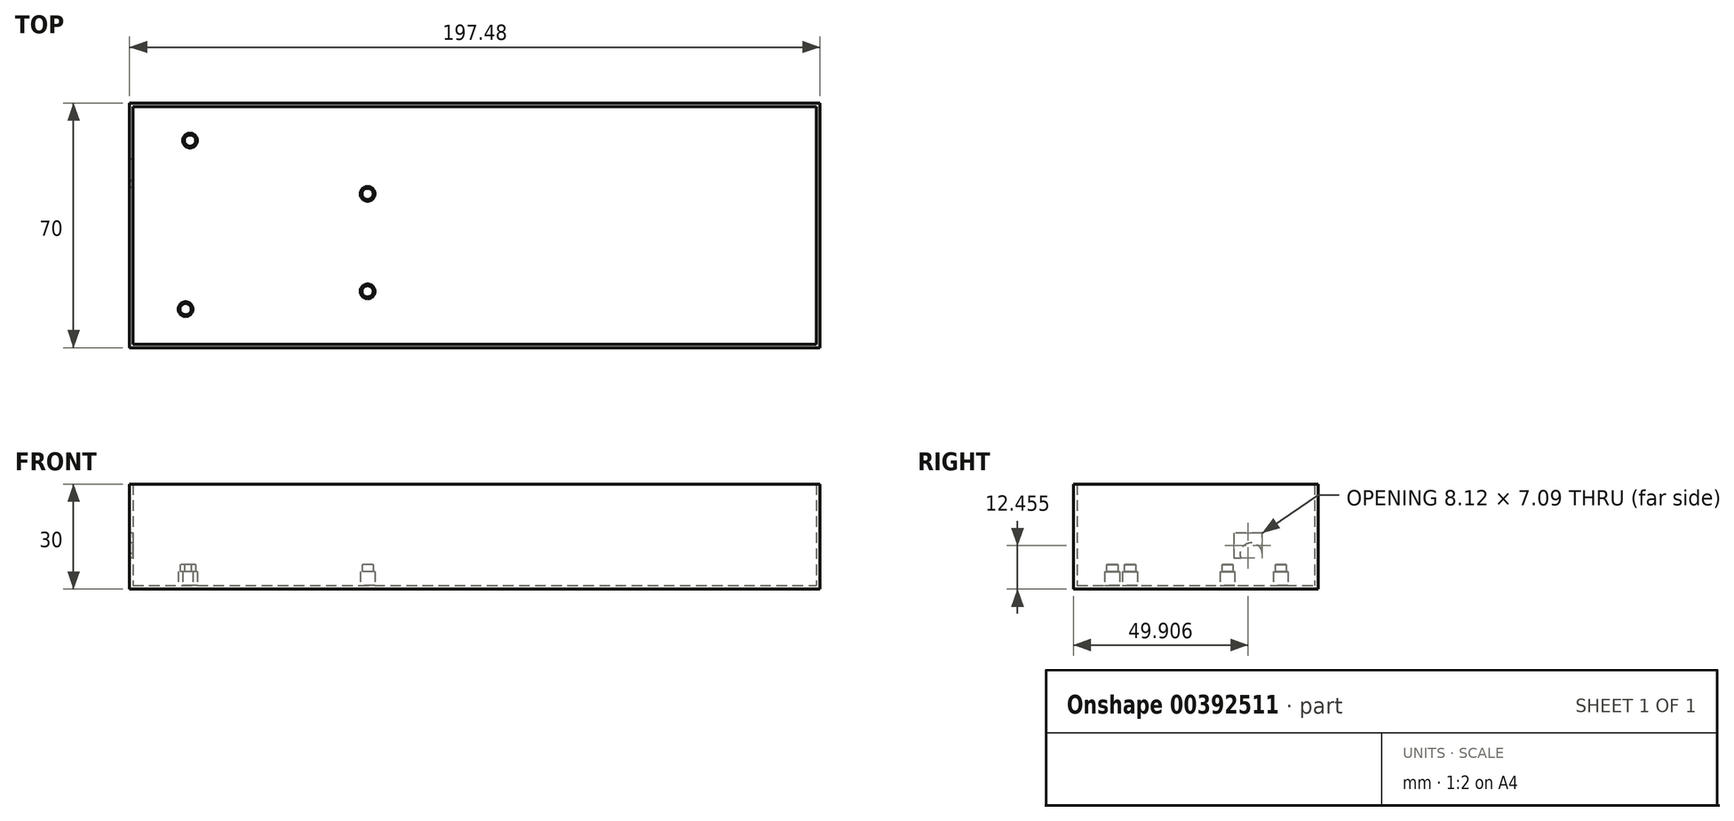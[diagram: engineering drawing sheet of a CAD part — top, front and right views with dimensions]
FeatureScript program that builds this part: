
annotation { "Feature Type Name" : "Feature", "Feature Type Description" : "" }
export const myFeature = defineFeature(function(context is Context, id is Id, definition is map)
    precondition{}
    {
        {
            var Q0;
            Q0=qCreatedBy(makeId("Top.planeOp"),FACE);
            var sketch = newSketch(context, id + "F0", { "sketchPlane" : qUnion([Q0])});
            skLineSegment(sketch, "E0", {"start": v(5.58, 61.8) * mm, "end": v(69.06, 61.8) * mm});
            skLineSegment(sketch, "E1", {"start": v(5.33, 61.76) * mm, "end": v(5.58, 61.8) * mm});
            skLineSegment(sketch, "E2", {"start": v(5.1, 61.65) * mm, "end": v(5.33, 61.76) * mm});
            skLineSegment(sketch, "E3", {"start": v(4.88, 61.5) * mm, "end": v(5.1, 61.65) * mm});
            skLineSegment(sketch, "E4", {"start": v(4.71, 61.3) * mm, "end": v(4.88, 61.5) * mm});
            skLineSegment(sketch, "E5", {"start": v(4.63, 61.06) * mm, "end": v(4.71, 61.3) * mm});
            skLineSegment(sketch, "E6", {"start": v(4.59, 60.79) * mm, "end": v(4.63, 61.06) * mm});
            skLineSegment(sketch, "E7", {"start": v(4.59, 9.5) * mm, "end": v(4.59, 60.79) * mm});
            skLineSegment(sketch, "E8", {"start": v(4.63, 9.24) * mm, "end": v(4.59, 9.5) * mm});
            skLineSegment(sketch, "E9", {"start": v(4.71, 9) * mm, "end": v(4.63, 9.24) * mm});
            skLineSegment(sketch, "E10", {"start": v(4.88, 8.8) * mm, "end": v(4.71, 9) * mm});
            skLineSegment(sketch, "E11", {"start": v(5.1, 8.63) * mm, "end": v(4.88, 8.8) * mm});
            skLineSegment(sketch, "E12", {"start": v(5.33, 8.54) * mm, "end": v(5.1, 8.63) * mm});
            skLineSegment(sketch, "E13", {"start": v(5.58, 8.5) * mm, "end": v(5.33, 8.54) * mm});
            skLineSegment(sketch, "E14", {"start": v(69.59, 8.5) * mm, "end": v(5.58, 8.5) * mm});
            skLineSegment(sketch, "E15", {"start": v(69.84, 8.54) * mm, "end": v(69.59, 8.5) * mm});
            skLineSegment(sketch, "E16", {"start": v(70.07, 8.63) * mm, "end": v(69.84, 8.54) * mm});
            skLineSegment(sketch, "E17", {"start": v(70.29, 8.8) * mm, "end": v(70.07, 8.63) * mm});
            skLineSegment(sketch, "E18", {"start": v(70.46, 9) * mm, "end": v(70.29, 8.8) * mm});
            skLineSegment(sketch, "E19", {"start": v(70.54, 9.24) * mm, "end": v(70.46, 9) * mm});
            skLineSegment(sketch, "E20", {"start": v(70.58, 9.5) * mm, "end": v(70.54, 9.24) * mm});
            skLineSegment(sketch, "E21", {"start": v(70.58, 11.04) * mm, "end": v(70.58, 9.5) * mm});
            skLineSegment(sketch, "E22", {"start": v(73.12, 13.58) * mm, "end": v(70.58, 11.04) * mm});
            skLineSegment(sketch, "E23", {"start": v(73.12, 46.31) * mm, "end": v(73.12, 13.58) * mm});
            skLineSegment(sketch, "E24", {"start": v(70.58, 48.85) * mm, "end": v(73.12, 46.31) * mm});
            skLineSegment(sketch, "E25", {"start": v(70.58, 60.28) * mm, "end": v(70.58, 48.85) * mm});
            skLineSegment(sketch, "E26", {"start": v(69.06, 61.8) * mm, "end": v(70.58, 60.28) * mm});
            skCircle(sketch, "E27", {"center": v(19.82, 59.26) * mm, "radius": 1.6 * mm});
            skCircle(sketch, "E28", {"center": v(70.58, 44.03) * mm, "radius": 1.6 * mm});
            skCircle(sketch, "E29", {"center": v(70.58, 16.12) * mm, "radius": 1.6 * mm});
            skCircle(sketch, "E30", {"center": v(18.55, 11.04) * mm, "radius": 1.6 * mm});
            skSolve(sketch);
        }
        {
            var Q0;
            Q0=qCreatedBy(makeId("Top.planeOp"),FACE);
            var sketch = newSketch(context, id + "F1", { "sketchPlane" : qUnion([Q0])});
            skLineSegment(sketch, "E31", {"start": v(-3.83, 44.58) * mm, "end": v(3.97, 44.58) * mm});
            skLineSegment(sketch, "E32", {"start": v(3.97, 44.58) * mm, "end": v(3.97, 36.46) * mm});
            skLineSegment(sketch, "E33", {"start": v(3.97, 36.46) * mm, "end": v(-3.83, 36.46) * mm});
            skLineSegment(sketch, "E34", {"start": v(-3.83, 36.46) * mm, "end": v(-3.83, 44.58) * mm});
            skLineSegment(sketch, "E35", {"start": v(-3.79, 49.08) * mm, "end": v(1.44, 49.08) * mm});
            skLineSegment(sketch, "E36", {"start": v(1.44, 50.7) * mm, "end": v(-3.79, 50.7) * mm});
            skLineSegment(sketch, "E37", {"start": v(-3.79, 47.45) * mm, "end": v(1.44, 47.45) * mm});
            skLineSegment(sketch, "E38", {"start": v(1.44, 45.85) * mm, "end": v(-3.79, 45.85) * mm});
            skLineSegment(sketch, "E39", {"start": v(-3.79, 52.34) * mm, "end": v(1.44, 52.34) * mm});
            skLineSegment(sketch, "E40", {"start": v(1.44, 53.97) * mm, "end": v(-3.79, 53.97) * mm});
            skLineSegment(sketch, "E41", {"start": v(-3.79, 55.17) * mm, "end": v(-3.79, 53.97) * mm});
            skLineSegment(sketch, "E42", {"start": v(-3.79, 53.97) * mm, "end": v(-3.79, 52.34) * mm});
            skLineSegment(sketch, "E43", {"start": v(-3.79, 52.34) * mm, "end": v(-3.79, 50.7) * mm});
            skLineSegment(sketch, "E44", {"start": v(-3.79, 50.7) * mm, "end": v(-3.79, 49.08) * mm});
            skLineSegment(sketch, "E45", {"start": v(-3.79, 49.08) * mm, "end": v(-3.79, 47.45) * mm});
            skLineSegment(sketch, "E46", {"start": v(-3.79, 47.45) * mm, "end": v(-3.79, 45.85) * mm});
            skLineSegment(sketch, "E47", {"start": v(-3.79, 45.85) * mm, "end": v(-3.79, 44.62) * mm});
            skLineSegment(sketch, "E48", {"start": v(-3.79, 44.62) * mm, "end": v(-5.18, 44.62) * mm});
            skLineSegment(sketch, "E49", {"start": v(-5.18, 44.62) * mm, "end": v(-5.18, 45.85) * mm});
            skLineSegment(sketch, "E50", {"start": v(-5.18, 45.85) * mm, "end": v(-5.18, 53.97) * mm});
            skLineSegment(sketch, "E51", {"start": v(-5.18, 53.97) * mm, "end": v(-5.18, 55.17) * mm});
            skLineSegment(sketch, "E52", {"start": v(-5.18, 55.17) * mm, "end": v(-3.79, 55.17) * mm});
            skLineSegment(sketch, "E53", {"start": v(-5.18, 45.85) * mm, "end": v(-6.81, 45.85) * mm});
            skLineSegment(sketch, "E54", {"start": v(-6.81, 45.85) * mm, "end": v(-7.68, 45.85) * mm});
            skLineSegment(sketch, "E55", {"start": v(-7.68, 45.85) * mm, "end": v(-8.08, 45.85) * mm});
            skLineSegment(sketch, "E56", {"start": v(-8.08, 45.85) * mm, "end": v(-8.44, 45.85) * mm});
            skLineSegment(sketch, "E57", {"start": v(-8.44, 45.85) * mm, "end": v(-8.88, 45.85) * mm});
            skLineSegment(sketch, "E58", {"start": v(-8.88, 45.85) * mm, "end": v(-9.29, 45.85) * mm});
            skLineSegment(sketch, "E59", {"start": v(-9.29, 45.85) * mm, "end": v(-9.7, 45.85) * mm});
            skLineSegment(sketch, "E60", {"start": v(-9.7, 45.85) * mm, "end": v(-10.07, 45.85) * mm});
            skLineSegment(sketch, "E61", {"start": v(-10.07, 45.85) * mm, "end": v(-10.51, 45.85) * mm});
            skLineSegment(sketch, "E62", {"start": v(-10.51, 45.85) * mm, "end": v(-10.91, 45.85) * mm});
            skLineSegment(sketch, "E63", {"start": v(-10.91, 45.85) * mm, "end": v(-11.68, 45.85) * mm});
            skLineSegment(sketch, "E64", {"start": v(-11.68, 45.85) * mm, "end": v(-14.17, 45.85) * mm});
            skLineSegment(sketch, "E65", {"start": v(-5.18, 53.97) * mm, "end": v(-8.08, 53.97) * mm});
            skLineSegment(sketch, "E66", {"start": v(-8.08, 53.97) * mm, "end": v(-8.88, 53.97) * mm});
            skLineSegment(sketch, "E67", {"start": v(-8.88, 53.97) * mm, "end": v(-9.7, 53.97) * mm});
            skLineSegment(sketch, "E68", {"start": v(-9.7, 53.97) * mm, "end": v(-10.51, 53.97) * mm});
            skLineSegment(sketch, "E69", {"start": v(-10.51, 53.97) * mm, "end": v(-11.32, 53.97) * mm});
            skLineSegment(sketch, "E70", {"start": v(-11.32, 53.97) * mm, "end": v(-12.14, 53.97) * mm});
            skLineSegment(sketch, "E71", {"start": v(-12.14, 53.97) * mm, "end": v(-12.95, 53.97) * mm});
            skLineSegment(sketch, "E72", {"start": v(-12.95, 53.97) * mm, "end": v(-14.17, 53.97) * mm});
            skLineSegment(sketch, "E73", {"start": v(-14.17, 45.85) * mm, "end": v(-14.17, 53.97) * mm});
            skLineSegment(sketch, "E74", {"start": v(-12.14, 53.97) * mm, "end": v(-10.87, 45.85) * mm});
            skLineSegment(sketch, "E75", {"start": v(-11.32, 53.97) * mm, "end": v(-10.07, 45.85) * mm});
            skLineSegment(sketch, "E76", {"start": v(-10.51, 53.97) * mm, "end": v(-9.24, 45.85) * mm});
            skLineSegment(sketch, "E77", {"start": v(-9.7, 53.97) * mm, "end": v(-8.44, 45.85) * mm});
            skLineSegment(sketch, "E78", {"start": v(-8.88, 53.97) * mm, "end": v(-7.62, 45.85) * mm});
            skLineSegment(sketch, "E79", {"start": v(-8.08, 53.97) * mm, "end": v(-6.81, 45.85) * mm});
            skLineSegment(sketch, "E80", {"start": v(-12.95, 53.97) * mm, "end": v(-11.68, 45.85) * mm});
            skLineSegment(sketch, "E81", {"start": v(-3.83, 34.95) * mm, "end": v(-3.83, 35.19) * mm});
            skLineSegment(sketch, "E82", {"start": v(-3.83, 35.19) * mm, "end": v(-3.83, 35.59) * mm});
            skLineSegment(sketch, "E83", {"start": v(-3.83, 35.59) * mm, "end": v(-2.2, 35.59) * mm});
            skLineSegment(sketch, "E84", {"start": v(0.04, 35.59) * mm, "end": v(0.8, 35.59) * mm});
            skLineSegment(sketch, "E85", {"start": v(0.8, 25.99) * mm, "end": v(0.04, 25.99) * mm});
            skLineSegment(sketch, "E86", {"start": v(-2.2, 25.99) * mm, "end": v(-3.83, 25.99) * mm});
            skLineSegment(sketch, "E87", {"start": v(-3.83, 25.99) * mm, "end": v(-3.83, 26.35) * mm});
            skLineSegment(sketch, "E88", {"start": v(-3.83, 26.35) * mm, "end": v(-3.83, 26.54) * mm});
            skLineSegment(sketch, "E89", {"start": v(-4.34, 34.55) * mm, "end": v(-4.34, 27.02) * mm});
            skLineSegment(sketch, "E90", {"start": v(-4.61, 34.55) * mm, "end": v(-4.61, 27.02) * mm});
            skLineSegment(sketch, "E91", {"start": v(-4.1, 34.7) * mm, "end": v(-4.06, 34.7) * mm});
            skLineSegment(sketch, "E92", {"start": v(-4.1, 34.7) * mm, "end": v(-4.42, 34.7) * mm});
            skLineSegment(sketch, "E93", {"start": v(-4.1, 26.8) * mm, "end": v(-4.06, 26.8) * mm});
            skLineSegment(sketch, "E94", {"start": v(-4.1, 26.8) * mm, "end": v(-4.42, 26.8) * mm});
            skLineSegment(sketch, "E95", {"start": v(-4.1, 34.7) * mm, "end": v(-3.98, 34.74) * mm});
            skLineSegment(sketch, "E96", {"start": v(-3.98, 34.74) * mm, "end": v(-3.83, 34.87) * mm});
            skLineSegment(sketch, "E97", {"start": v(-3.83, 34.87) * mm, "end": v(-3.83, 34.95) * mm});
            skLineSegment(sketch, "E98", {"start": v(-4.1, 34.7) * mm, "end": v(-4.23, 34.7) * mm});
            skLineSegment(sketch, "E99", {"start": v(-4.23, 34.7) * mm, "end": v(-4.34, 34.66) * mm});
            skLineSegment(sketch, "E100", {"start": v(-4.34, 34.66) * mm, "end": v(-4.34, 34.51) * mm});
            skLineSegment(sketch, "E101", {"start": v(-4.38, 34.7) * mm, "end": v(-4.5, 34.7) * mm});
            skLineSegment(sketch, "E102", {"start": v(-4.5, 34.7) * mm, "end": v(-4.61, 34.66) * mm});
            skLineSegment(sketch, "E103", {"start": v(-4.61, 34.66) * mm, "end": v(-4.61, 34.51) * mm});
            skLineSegment(sketch, "E104", {"start": v(-4.61, 27.02) * mm, "end": v(-4.61, 26.9) * mm});
            skLineSegment(sketch, "E105", {"start": v(-4.61, 26.9) * mm, "end": v(-4.5, 26.83) * mm});
            skLineSegment(sketch, "E106", {"start": v(-4.5, 26.83) * mm, "end": v(-4.38, 26.8) * mm});
            skLineSegment(sketch, "E107", {"start": v(-4.34, 27.02) * mm, "end": v(-4.34, 26.9) * mm});
            skLineSegment(sketch, "E108", {"start": v(-4.34, 26.9) * mm, "end": v(-4.23, 26.83) * mm});
            skLineSegment(sketch, "E109", {"start": v(-4.23, 26.83) * mm, "end": v(-4.1, 26.8) * mm});
            skLineSegment(sketch, "E110", {"start": v(-3.83, 26.54) * mm, "end": v(-3.83, 26.7) * mm});
            skLineSegment(sketch, "E111", {"start": v(-3.83, 26.7) * mm, "end": v(-3.98, 26.75) * mm});
            skLineSegment(sketch, "E112", {"start": v(-3.98, 26.75) * mm, "end": v(-4.1, 26.8) * mm});
            skLineSegment(sketch, "E113", {"start": v(-3.83, 35.55) * mm, "end": v(-4.42, 35.9) * mm});
            skLineSegment(sketch, "E114", {"start": v(-4.38, 35.9) * mm, "end": v(-4.61, 35.55) * mm});
            skLineSegment(sketch, "E115", {"start": v(-4.61, 35.59) * mm, "end": v(-4.02, 35.19) * mm});
            skLineSegment(sketch, "E116", {"start": v(-4.02, 35.19) * mm, "end": v(-3.83, 35.19) * mm});
            skLineSegment(sketch, "E117", {"start": v(-3.83, 25.99) * mm, "end": v(-4.42, 25.67) * mm});
            skLineSegment(sketch, "E118", {"start": v(-4.38, 25.67) * mm, "end": v(-4.61, 25.99) * mm});
            skLineSegment(sketch, "E119", {"start": v(-4.61, 25.99) * mm, "end": v(-4.02, 26.3) * mm});
            skLineSegment(sketch, "E120", {"start": v(-3.83, 26.35) * mm, "end": v(-4.02, 26.3) * mm});
            skLineSegment(sketch, "E121", {"start": v(-5.54, 16.6) * mm, "end": v(-5.54, 5.37) * mm});
            skLineSegment(sketch, "E122", {"start": v(11.46, 16.6) * mm, "end": v(-1.04, 16.6) * mm});
            skLineSegment(sketch, "E123", {"start": v(-1.04, 16.6) * mm, "end": v(-5.54, 16.6) * mm});
            skLineSegment(sketch, "E124", {"start": v(-5.54, 5.37) * mm, "end": v(4.42, 5.37) * mm});
            skLineSegment(sketch, "E125", {"start": v(-1.04, 16.6) * mm, "end": v(-1.04, 5.37) * mm});
            skLineSegment(sketch, "E126", {"start": v(-5.01, 14.84) * mm, "end": v(-3.75, 14.84) * mm});
            skLineSegment(sketch, "E127", {"start": v(-3.11, 14.84) * mm, "end": v(-1.8, 14.84) * mm});
            skLineSegment(sketch, "E128", {"start": v(-0.55, 14.84) * mm, "end": v(0.76, 14.84) * mm});
            skLineSegment(sketch, "E129", {"start": v(-5.01, 7.12) * mm, "end": v(-3.75, 7.12) * mm});
            skLineSegment(sketch, "E130", {"start": v(-3.11, 7.12) * mm, "end": v(-1.8, 7.12) * mm});
            skLineSegment(sketch, "E131", {"start": v(-0.55, 7.12) * mm, "end": v(0.76, 7.12) * mm});
            skLineSegment(sketch, "E132", {"start": v(1.4, 7.12) * mm, "end": v(2.66, 7.12) * mm});
            skLineSegment(sketch, "E133", {"start": v(3.3, 7.12) * mm, "end": v(4.6, 7.12) * mm});
            skLineSegment(sketch, "E134", {"start": v(-4.34, 12.22) * mm, "end": v(-1.8, 12.22) * mm});
            skLineSegment(sketch, "E135", {"start": v(-0.55, 12.22) * mm, "end": v(2.66, 12.22) * mm});
            skLineSegment(sketch, "E136", {"start": v(-4.34, 9.7) * mm, "end": v(-1.8, 9.7) * mm});
            skLineSegment(sketch, "E137", {"start": v(-0.55, 9.7) * mm, "end": v(2.66, 9.7) * mm});
            skLineSegment(sketch, "E138", {"start": v(-4.34, 12.22) * mm, "end": v(-5.01, 11.65) * mm});
            skLineSegment(sketch, "E139", {"start": v(-5.01, 11.65) * mm, "end": v(-5.01, 10.34) * mm});
            skLineSegment(sketch, "E140", {"start": v(-5.01, 10.34) * mm, "end": v(-4.34, 9.7) * mm});
            skLineSegment(sketch, "E141", {"start": v(4.42, 6.53) * mm, "end": v(3.57, 6.53) * mm});
            skLineSegment(sketch, "E142", {"start": v(3.57, 6.53) * mm, "end": v(3.57, 15.48) * mm});
            skLineSegment(sketch, "E143", {"start": v(0, 9.07) * mm, "end": v(0.8, 7.84) * mm});
            skLineSegment(sketch, "E144", {"start": v(0.8, 9.07) * mm, "end": v(0, 7.84) * mm});
            skLineSegment(sketch, "E145", {"start": v(1.8, 7.84) * mm, "end": v(1.8, 9.07) * mm});
            skLineSegment(sketch, "E146", {"start": v(1.86, 9.07) * mm, "end": v(1.18, 8.43) * mm});
            skLineSegment(sketch, "E147", {"start": v(1.18, 8.43) * mm, "end": v(1.99, 8.43) * mm});
            skLineSegment(sketch, "E148", {"start": v(78.58, 69.21) * mm, "end": v(80.57, 67.23) * mm});
            skLineSegment(sketch, "E149", {"start": v(80.53, 52.7) * mm, "end": v(83.79, 49.44) * mm});
            skLineSegment(sketch, "E150", {"start": v(83.79, 49.44) * mm, "end": v(83.79, 7.59) * mm});
            skLineSegment(sketch, "E151", {"start": v(83.79, 7.59) * mm, "end": v(80.53, 4.33) * mm});
            skLineSegment(sketch, "E152", {"start": v(80.53, 4.33) * mm, "end": v(80.53, 2.39) * mm});
            skLineSegment(sketch, "E153", {"start": v(79.26, 1.08) * mm, "end": v(79.62, 1.12) * mm});
            skLineSegment(sketch, "E154", {"start": v(79.62, 1.12) * mm, "end": v(80.04, 1.35) * mm});
            skLineSegment(sketch, "E155", {"start": v(80.04, 1.35) * mm, "end": v(80.3, 1.63) * mm});
            skLineSegment(sketch, "E156", {"start": v(80.3, 1.63) * mm, "end": v(80.49, 1.94) * mm});
            skLineSegment(sketch, "E157", {"start": v(80.49, 1.94) * mm, "end": v(80.57, 2.39) * mm});
            skLineSegment(sketch, "E158", {"start": v(79.26, 1.08) * mm, "end": v(-2.58, 1.08) * mm});
            skLineSegment(sketch, "E159", {"start": v(-3.83, 2.39) * mm, "end": v(-3.79, 1.94) * mm});
            skLineSegment(sketch, "E160", {"start": v(-3.79, 1.94) * mm, "end": v(-3.56, 1.63) * mm});
            skLineSegment(sketch, "E161", {"start": v(-3.56, 1.63) * mm, "end": v(-3.3, 1.35) * mm});
            skLineSegment(sketch, "E162", {"start": v(-3.3, 1.35) * mm, "end": v(-2.98, 1.12) * mm});
            skLineSegment(sketch, "E163", {"start": v(-2.98, 1.12) * mm, "end": v(-2.52, 1.08) * mm});
            skLineSegment(sketch, "E164", {"start": v(-2.52, 69.21) * mm, "end": v(-2.98, 69.17) * mm});
            skLineSegment(sketch, "E165", {"start": v(-2.98, 69.17) * mm, "end": v(-3.3, 68.98) * mm});
            skLineSegment(sketch, "E166", {"start": v(-3.3, 68.98) * mm, "end": v(-3.56, 68.7) * mm});
            skLineSegment(sketch, "E167", {"start": v(-3.56, 68.7) * mm, "end": v(-3.79, 68.35) * mm});
            skLineSegment(sketch, "E168", {"start": v(-3.79, 68.35) * mm, "end": v(-3.83, 67.95) * mm});
            skLineSegment(sketch, "E169", {"start": v(-2.58, 69.21) * mm, "end": v(78.58, 69.21) * mm});
            skLineSegment(sketch, "E170", {"start": v(80.53, 67.23) * mm, "end": v(80.53, 52.7) * mm});
            skLineSegment(sketch, "E171", {"start": v(-3.83, 67.9) * mm, "end": v(-3.83, 2.39) * mm});
            skCircle(sketch, "E172", {"center": v(8.67, 4.72) * mm, "radius": 1.5 * mm});
            skSolve(sketch);
        }
        {
            var Q0;
            Q0=qCreatedBy(makeId("Top.planeOp"),FACE);
            var sketch = newSketch(context, id + "F2", { "sketchPlane" : qUnion([Q0])});
            skLineSegment(sketch, "E173.bottom", {"start": v(3.52, 0) * mm, "end": v(200, 0) * mm});
            skLineSegment(sketch, "E173.top", {"start": v(3.52, 70) * mm, "end": v(200, 70) * mm});
            skLineSegment(sketch, "E173.right", {"start": v(200, 0) * mm, "end": v(200, 70) * mm});
            skLineSegment(sketch, "E174", {"start": v(3.52, 0) * mm, "end": v(3.52, 70) * mm});
            skCircle(sketch, "E175.0", {"center": v(19.82, 59.26) * mm, "radius": 1.6 * mm});
            skCircle(sketch, "E176.0", {"center": v(18.55, 11.04) * mm, "radius": 1.6 * mm});
            skCircle(sketch, "E177.0", {"center": v(70.58, 16.12) * mm, "radius": 1.6 * mm});
            skCircle(sketch, "E178.0", {"center": v(70.58, 44.03) * mm, "radius": 1.6 * mm});
            skCircle(sketch, "E179.0", {"center": v(19.82, 59.26) * mm, "radius": 2.1 * mm});
            skCircle(sketch, "E180.0", {"center": v(18.55, 11.04) * mm, "radius": 2.1 * mm});
            skCircle(sketch, "E181.0", {"center": v(70.58, 44.03) * mm, "radius": 2.1 * mm});
            skCircle(sketch, "E182.0", {"center": v(70.58, 16.12) * mm, "radius": 2.1 * mm});
            skLineSegment(sketch, "E183.0", {"start": v(2.52, 0) * mm, "end": v(2.52, 70) * mm});
            skLineSegment(sketch, "E184", {"start": v(2.52, 70) * mm, "end": v(3.52, 70) * mm});
            skLineSegment(sketch, "E185", {"start": v(2.52, 0) * mm, "end": v(3.52, 0) * mm});
            skLineSegment(sketch, "E186.0", {"start": v(3.52, 69) * mm, "end": v(200, 69) * mm});
            skLineSegment(sketch, "E187.0", {"start": v(199, 0) * mm, "end": v(199, 70) * mm});
            skLineSegment(sketch, "E188.0", {"start": v(3.52, 1) * mm, "end": v(200, 1) * mm});
            skSolve(sketch);
        }
        {
            var Q0;
            Q0=makeQuery(id+"F2.imprint","IMPRINT",FACE,{"disambiguationData":[TD([[makeQuery(id+"F2.imprint","IMPRINT",EDGE,{"derivedFrom":sQuery(id+"F2.wireOp",EDGE,"E179.0")}),-1.0]])]});
            extrude(context, id + "F3", {"entities" : qUnion([Q0]), "depth" : 1 * mm});
        }
        {
            var Q0;
            Q0=makeQuery(id+"F2.imprint","IMPRINT",FACE,{"disambiguationData":[TD([[makeQuery(id+"F2.imprint","IMPRINT",EDGE,{"derivedFrom":sQuery(id+"F2.wireOp",EDGE,"E175.0")}),-1.0]])]});
            var Q1;
            Q1=makeQuery(id+"F2.imprint","IMPRINT",FACE,{"disambiguationData":[TD([[makeQuery(id+"F2.imprint","IMPRINT",EDGE,{"derivedFrom":sQuery(id+"F2.wireOp",EDGE,"E178.0")}),-1.0]])]});
            var Q2;
            Q2=makeQuery(id+"F2.imprint","IMPRINT",FACE,{"disambiguationData":[TD([[makeQuery(id+"F2.imprint","IMPRINT",EDGE,{"derivedFrom":sQuery(id+"F2.wireOp",EDGE,"E177.0")}),-1.0]])]});
            var Q3;
            Q3=makeQuery(id+"F2.imprint","IMPRINT",FACE,{"disambiguationData":[TD([[makeQuery(id+"F2.imprint","IMPRINT",EDGE,{"derivedFrom":sQuery(id+"F2.wireOp",EDGE,"E176.0")}),-1.0]])]});
            extrude(context, id + "F4", {"entities" : qUnion([Q0, Q1, Q2, Q3]), "operationType" : NewBodyOperationType.ADD, "depth" : 5 * mm});
        }
        {
            var Q0;
            Q0=makeQuery(id+"F2.imprint","IMPRINT",FACE,{"disambiguationData":[TD([[makeQuery(id+"F2.imprint","IMPRINT",EDGE,{"derivedFrom":sQuery(id+"F2.wireOp",EDGE,"E175.0")}),1.0]])]});
            var Q1;
            Q1=makeQuery(id+"F2.imprint","IMPRINT",FACE,{"disambiguationData":[TD([[makeQuery(id+"F2.imprint","IMPRINT",EDGE,{"derivedFrom":sQuery(id+"F2.wireOp",EDGE,"E178.0")}),1.0]])]});
            var Q2;
            Q2=makeQuery(id+"F2.imprint","IMPRINT",FACE,{"disambiguationData":[TD([[makeQuery(id+"F2.imprint","IMPRINT",EDGE,{"derivedFrom":sQuery(id+"F2.wireOp",EDGE,"E177.0")}),1.0]])]});
            var Q3;
            Q3=makeQuery(id+"F2.imprint","IMPRINT",FACE,{"disambiguationData":[TD([[makeQuery(id+"F2.imprint","IMPRINT",EDGE,{"derivedFrom":sQuery(id+"F2.wireOp",EDGE,"E176.0")}),1.0]])]});
            extrude(context, id + "F5", {"entities" : qUnion([Q0, Q1, Q2, Q3]), "operationType" : NewBodyOperationType.ADD, "depth" : 7 * mm});
        }
        {
            var Q0;
            {var subQ0=sQuery(id+"F2.wireOp",EDGE,"E174");var subQ5=sQuery(id+"F2.wireOp",EDGE,"E186.0");var subQ6=makeQuery(id+"F2.imprint","INTERSECT",VERTEX,{"derivedFrom":[subQ0,subQ5]});Q0=makeQuery(id+"F2.imprint","IMPRINT",FACE,{"disambiguationData":[TD([[makeQuery(id+"F2.imprint","IMPRINT",EDGE,{"disambiguationData":[TD([[subQ6,-1.0]])],"derivedFrom":subQ5}),1.0]])]});}
            var Q1;
            {var subQ0=sQuery(id+"F2.wireOp",EDGE,"E173.right");var subQ1=sQuery(id+"F2.wireOp",EDGE,"E173.top");var subQ2=makeQuery(id+"F2.imprint","INTERSECT",VERTEX,{"derivedFrom":[subQ1,subQ0]});Q1=makeQuery(id+"F2.imprint","IMPRINT",FACE,{"disambiguationData":[TD([[makeQuery(id+"F2.imprint","IMPRINT",EDGE,{"disambiguationData":[TD([[subQ2,1.0]])],"derivedFrom":subQ1}),-1.0]])]});}
            var Q2;
            Q2=makeQuery(id+"F2.imprint","IMPRINT",FACE,{"disambiguationData":[TD([[makeQuery(id+"F2.imprint","IMPRINT",EDGE,{"derivedFrom":sQuery(id+"F2.wireOp",EDGE,"E183.0")}),-1.0]])]});
            var Q3;
            {var subQ1=sQuery(id+"F2.wireOp",EDGE,"E173.bottom");var subQ3=sQuery(id+"F2.wireOp",EDGE,"E187.0");var subQ4=makeQuery(id+"F2.imprint","INTERSECT",VERTEX,{"derivedFrom":[subQ1,subQ3]});Q3=makeQuery(id+"F2.imprint","IMPRINT",FACE,{"disambiguationData":[TD([[makeQuery(id+"F2.imprint","IMPRINT",EDGE,{"disambiguationData":[TD([[subQ4,-1.0]])],"derivedFrom":subQ3}),1.0]])]});}
            var Q4;
            {var subQ0=sQuery(id+"F2.wireOp",EDGE,"E173.right");var subQ1=sQuery(id+"F2.wireOp",EDGE,"E173.bottom");var subQ2=makeQuery(id+"F2.imprint","INTERSECT",VERTEX,{"derivedFrom":[subQ1,subQ0]});Q4=makeQuery(id+"F2.imprint","IMPRINT",FACE,{"disambiguationData":[TD([[makeQuery(id+"F2.imprint","IMPRINT",EDGE,{"disambiguationData":[TD([[subQ2,1.0]])],"derivedFrom":subQ1}),1.0]])]});}
            var Q5;
            {var subQ0=sQuery(id+"F2.wireOp",EDGE,"E186.0");var subQ1=sQuery(id+"F2.wireOp",EDGE,"E173.right");var subQ2=makeQuery(id+"F2.imprint","INTERSECT",VERTEX,{"derivedFrom":[subQ1,subQ0]});Q5=makeQuery(id+"F2.imprint","IMPRINT",FACE,{"disambiguationData":[TD([[makeQuery(id+"F2.imprint","IMPRINT",EDGE,{"disambiguationData":[TD([[subQ2,1.0]])],"derivedFrom":subQ1}),1.0]])]});}
            extrude(context, id + "F6", {"entities" : qUnion([Q0, Q1, Q2, Q3, Q4, Q5]), "operationType" : NewBodyOperationType.ADD, "depth" : 30 * mm});
        }
        {
            var Q0;
            Q0=makeQuery(id+"F6.opExtrude","SWEPT_FACE",FACE,{"disambiguationData":[OSD([sQuery(id+"F2.wireOp",EDGE,"E183.0")])]});
            var sketch = newSketch(context, id + "F7", { "sketchPlane" : qUnion([Q0])});
            skLineSegment(sketch, "E189.0", {"start": v(0, 0) * mm, "end": v(-70, 0) * mm});
            skLineSegment(sketch, "E189.1", {"start": v(0, 30) * mm, "end": v(0, 10) * mm});
            skLineSegment(sketch, "E190.0", {"start": v(0, 30) * mm, "end": v(-70, 30) * mm});
            skLineSegment(sketch, "E191.0", {"start": v(-70, 30) * mm, "end": v(-70, 0) * mm});
            skLineSegment(sketch, "E192", {"start": v(0, 6) * mm, "end": v(-70, 6) * mm});
            skLineSegment(sketch, "E193", {"start": v(-45.85, 0) * mm, "end": v(-53.97, 0) * mm});
            skLineSegment(sketch, "E194", {"start": v(-53.97, 0) * mm, "end": v(-53.97, 16) * mm});
            skLineSegment(sketch, "E195", {"start": v(-53.97, 16) * mm, "end": v(-45.85, 16) * mm});
            skLineSegment(sketch, "E196", {"start": v(-45.85, 16) * mm, "end": v(-45.85, 0) * mm});
            skLineSegment(sketch, "E197", {"start": v(-45.85, 6) * mm, "end": v(-45.85, 7) * mm});
            skLineSegment(sketch, "E198", {"start": v(-45.85, 7) * mm, "end": v(-53.97, 7) * mm});
            skLineSegment(sketch, "E199", {"start": v(-38.21, 8.9) * mm, "end": v(-53.9, 8.9) * mm});
            skCircle(sketch, "E200", {"center": v(-50.8, 10.03) * mm, "radius": 3.16 * mm});
            skPoint(sketch, "E200.first.point", {"position": v(-49.9, 7) * mm});
            skPoint(sketch, "E200.second.point", {"position": v(-49.9, 13.07) * mm});
            skPoint(sketch, "E200.second.point.positionSnap0", {"position": v(-49.9, 16) * mm});
            skPoint(sketch, "E200.third.point", {"position": v(-53.97, 9.95) * mm});
            skSolve(sketch);
        }
        {
            var Q0;
            {var subQ0=sQuery(id+"F7.wireOp",EDGE,"E200");var subQ1=sQuery(id+"F7.wireOp",EDGE,"E199");var subQ2=makeQuery(id+"F7.imprint","INTERSECT",VERTEX,{"disambiguationData":[OD(0.0)],"derivedFrom":[subQ1,subQ0]});Q0=makeQuery(id+"F7.imprint","IMPRINT",FACE,{"disambiguationData":[TD([[makeQuery(id+"F7.imprint","IMPRINT",EDGE,{"disambiguationData":[TD([[subQ2,-1.0]])],"derivedFrom":subQ1}),1.0]])]});}
            var Q1;
            {var subQ0=sQuery(id+"F7.wireOp",EDGE,"E200");var subQ1=sQuery(id+"F7.wireOp",EDGE,"E194");var subQ2=makeQuery(id+"F7.imprint","INTERSECT",VERTEX,{"disambiguationData":[OD(0.0)],"derivedFrom":[subQ1,subQ0]});Q1=makeQuery(id+"F7.imprint","IMPRINT",FACE,{"disambiguationData":[TD([[makeQuery(id+"F7.imprint","IMPRINT",EDGE,{"disambiguationData":[TD([[subQ2,-1.0]])],"derivedFrom":subQ1}),-1.0]])]});}
            extrude(context, id + "F8", {"entities" : qUnion([Q0, Q1]), "operationType" : NewBodyOperationType.REMOVE, "oppositeDirection" : true, "depth" : 1 * mm});
        }
    });
